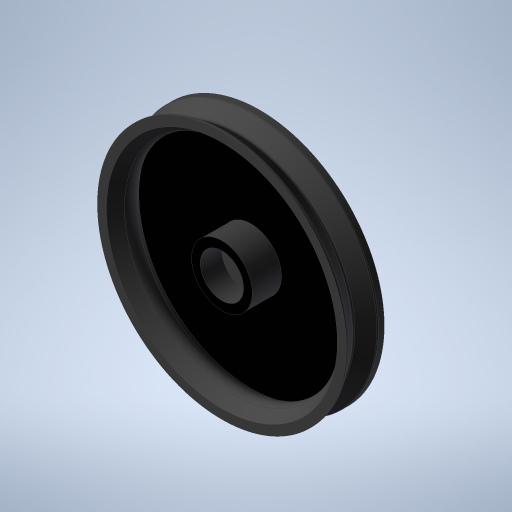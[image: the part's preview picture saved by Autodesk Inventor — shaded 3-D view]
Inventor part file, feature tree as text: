
AUTODESK INVENTOR PART (.ipt)
format: ipt  version: 2024.2 (Build 282272000, 272)  size: 314,880 bytes
history: native  units: mm
features: sketch x4, extrude x3, revolve x1, shell x1, projected_geometry x1
ambient origin geometry x8: Origin, YZ Plane, XZ Plane, XY Plane, X Axis, Y Axis, Z Axis, Center Point
bodies: Body1 (feature_tree)
feature tree (10):
  revolve  "Вращение2"
  shell  "Оболочка1"  Thickness=3.1mm
  extrude  "Выдавливание1"  Depth=0.2mm
  extrude  "Выдавливание4"  Depth=0.2mm
  extrude  "Выдавливание5"  Depth=1.55mm
  sketch  "Эскиз1"
  sketch  "Эскиз2"
  sketch  "Эскиз3"
  projected_geometry  "Спроецированная петля1"
  sketch  "Эскиз4"
